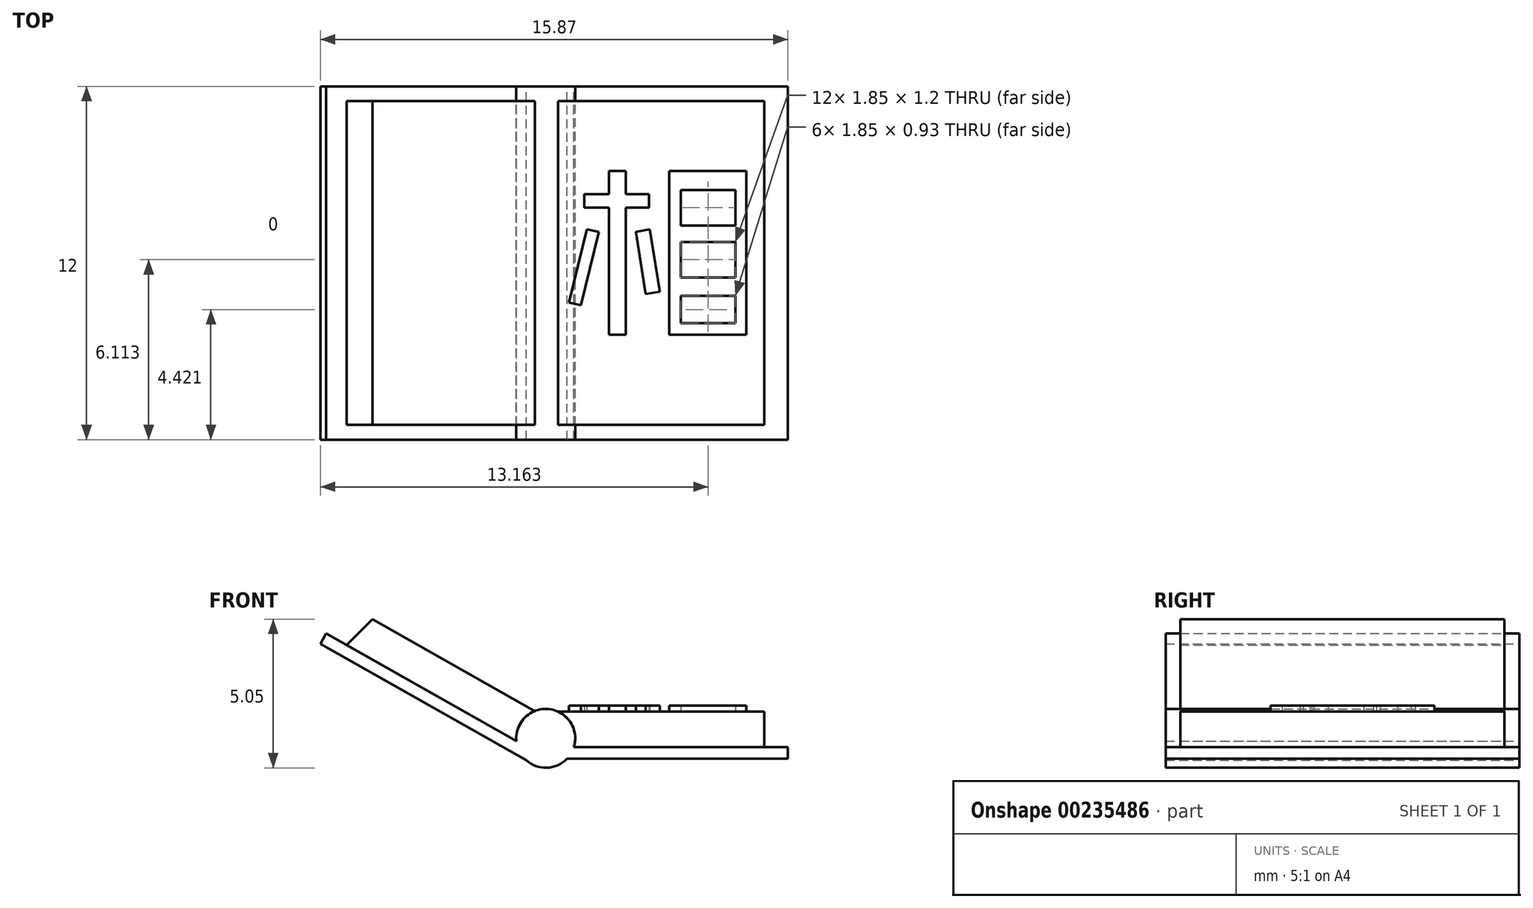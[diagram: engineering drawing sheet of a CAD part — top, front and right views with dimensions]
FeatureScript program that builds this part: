
annotation { "Feature Type Name" : "Feature", "Feature Type Description" : "" }
export const myFeature = defineFeature(function(context is Context, id is Id, definition is map)
    precondition{}
    {
        {
            var Q0;
            Q0=qCreatedBy(makeId("Front.planeOp"),FACE);
            var sketch = newSketch(context, id + "F0", { "sketchPlane" : qUnion([Q0])});
            skLineSegment(sketch, "E0", {"start": v(0.72, 0) * mm, "end": v(8.22, 0) * mm});
            skLineSegment(sketch, "E1", {"start": v(8.22, 0) * mm, "end": v(8.22, 0.4) * mm});
            skLineSegment(sketch, "E2", {"start": v(8.22, 0.4) * mm, "end": v(7.42, 0.4) * mm});
            skLineSegment(sketch, "E3", {"start": v(7.42, 0.4) * mm, "end": v(7.42, 1.6) * mm});
            skLineSegment(sketch, "E4", {"start": v(7.42, 1.6) * mm, "end": v(0.42, 1.6) * mm});
            skCircle(sketch, "E5", {"center": v(0, 0.7) * mm, "radius": 1 * mm});
            skPoint(sketch, "E6.orphan", {"position": v(0, 0) * mm});
            skLineSegment(sketch, "E7", {"start": v(7.42, 0.4) * mm, "end": v(0.96, 0.4) * mm});
            skLineSegment(sketch, "E8", {"start": v(7.42, 0.8) * mm, "end": v(1, 0.8) * mm});
            skLineSegment(sketch, "E9", {"start": v(7.42, 1.2) * mm, "end": v(0.86, 1.2) * mm});
            skLineSegment(sketch, "E10.1.0", {"start": v(-6.46, 4.15) * mm, "end": v(-0.94, 1.02) * mm});
            skLineSegment(sketch, "E10.1.2", {"start": v(-6.17, 4.45) * mm, "end": v(-0.74, 1.37) * mm});
            skLineSegment(sketch, "E10.1.3", {"start": v(-5.88, 4.74) * mm, "end": v(-0.37, 1.62) * mm});
            skLineSegment(sketch, "E10.1.5", {"start": v(-6.76, 3.86) * mm, "end": v(-1, 0.6) * mm});
            skLineSegment(sketch, "E10.1.8", {"start": v(-5.88, 4.74) * mm, "end": v(-6.76, 3.86) * mm});
            skLineSegment(sketch, "E10.anchor1", {"start": v(0, 0.7) * mm, "end": v(0.72, 0) * mm, "construction": true});
            skLineSegment(sketch, "E10.anchor2", {"start": v(0, 0.7) * mm, "end": v(-0.97, 0.93) * mm, "construction": true});
            skLineSegment(sketch, "E11.1.0", {"start": v(-0.67, -0.05) * mm, "end": v(-7.65, 3.9) * mm});
            skLineSegment(sketch, "E12", {"start": v(-6.76, 3.86) * mm, "end": v(-7.45, 4.25) * mm});
            skLineSegment(sketch, "E13", {"start": v(-7.45, 4.25) * mm, "end": v(-7.65, 3.9) * mm});
            skSolve(sketch);
        }
        {
            var Q0;
            {var subQ0=sQuery(id+"F0.wireOp",EDGE,"E5");var subQ5=makeQuery(id+"F0.imprint","INTERSECT",VERTEX,{"derivedFrom":[subQ0,sQuery(id+"F0.wireOp",EDGE,"E8")]});Q0=makeQuery(id+"F0.imprint","IMPRINT",FACE,{"disambiguationData":[TD([[makeQuery(id+"F0.imprint","IMPRINT",EDGE,{"disambiguationData":[TD([[subQ5,-1.0]])],"derivedFrom":subQ0}),1.0]])]});}
            var Q1;
            {var subQ1=sQuery(id+"F0.wireOp",EDGE,"E0");Q1=makeQuery(id+"F0.imprint","IMPRINT",FACE,{"disambiguationData":[TD([[makeQuery(id+"F0.imprint","IMPRINT",EDGE,{"derivedFrom":subQ1}),1.0]])]});}
            var Q2;
            {var subQ0=sQuery(id+"F0.wireOp",EDGE,"E10.1.5");Q2=makeQuery(id+"F0.imprint","IMPRINT",FACE,{"disambiguationData":[TD([[makeQuery(id+"F0.imprint","IMPRINT",EDGE,{"derivedFrom":subQ0}),-1.0]])]});}
            extrude(context, id + "F1", {"entities" : qUnion([Q0, Q1, Q2]), "depth" : 12 * mm});
        }
        {
            var Q0;
            {var subQ0=sQuery(id+"F0.wireOp",EDGE,"E7");Q0=makeQuery(id+"F0.imprint","IMPRINT",FACE,{"disambiguationData":[TD([[makeQuery(id+"F0.imprint","IMPRINT",EDGE,{"derivedFrom":subQ0}),-1.0]])]});}
            var Q1;
            {var subQ0=sQuery(id+"F0.wireOp",EDGE,"E8");Q1=makeQuery(id+"F0.imprint","IMPRINT",FACE,{"disambiguationData":[TD([[makeQuery(id+"F0.imprint","IMPRINT",EDGE,{"derivedFrom":subQ0}),-1.0]])]});}
            var Q2;
            {var subQ0=sQuery(id+"F0.wireOp",EDGE,"E4");Q2=makeQuery(id+"F0.imprint","IMPRINT",FACE,{"disambiguationData":[TD([[makeQuery(id+"F0.imprint","IMPRINT",EDGE,{"derivedFrom":subQ0}),1.0]])]});}
            var Q3;
            {var subQ0=sQuery(id+"F0.wireOp",EDGE,"E10.1.0");Q3=makeQuery(id+"F0.imprint","IMPRINT",FACE,{"disambiguationData":[TD([[makeQuery(id+"F0.imprint","IMPRINT",EDGE,{"derivedFrom":subQ0}),-1.0]])]});}
            var Q4;
            {var subQ0=sQuery(id+"F0.wireOp",EDGE,"E10.1.0");Q4=makeQuery(id+"F0.imprint","IMPRINT",FACE,{"disambiguationData":[TD([[makeQuery(id+"F0.imprint","IMPRINT",EDGE,{"derivedFrom":subQ0}),1.0]])]});}
            var Q5;
            {var subQ0=sQuery(id+"F0.wireOp",EDGE,"E10.1.2");Q5=makeQuery(id+"F0.imprint","IMPRINT",FACE,{"disambiguationData":[TD([[makeQuery(id+"F0.imprint","IMPRINT",EDGE,{"derivedFrom":subQ0}),1.0]])]});}
            extrude(context, id + "F2", {"entities" : qUnion([Q0, Q1, Q2, Q3, Q4, Q5]), "depth" : 11.5 * mm});
        }
        {
            var Q0;
            {var subQ0=sQuery(id+"F0.wireOp",EDGE,"E10.1.2");Q0=makeQuery(id+"F0.imprint","IMPRINT",FACE,{"disambiguationData":[TD([[makeQuery(id+"F0.imprint","IMPRINT",EDGE,{"derivedFrom":subQ0}),1.0]])]});}
            var Q1;
            {var subQ0=sQuery(id+"F0.wireOp",EDGE,"E10.1.0");Q1=makeQuery(id+"F0.imprint","IMPRINT",FACE,{"disambiguationData":[TD([[makeQuery(id+"F0.imprint","IMPRINT",EDGE,{"derivedFrom":subQ0}),1.0]])]});}
            var Q2;
            {var subQ0=sQuery(id+"F0.wireOp",EDGE,"E10.1.0");Q2=makeQuery(id+"F0.imprint","IMPRINT",FACE,{"disambiguationData":[TD([[makeQuery(id+"F0.imprint","IMPRINT",EDGE,{"derivedFrom":subQ0}),-1.0]])]});}
            var Q3;
            {var subQ0=sQuery(id+"F0.wireOp",EDGE,"E4");Q3=makeQuery(id+"F0.imprint","IMPRINT",FACE,{"disambiguationData":[TD([[makeQuery(id+"F0.imprint","IMPRINT",EDGE,{"derivedFrom":subQ0}),1.0]])]});}
            var Q4;
            {var subQ0=sQuery(id+"F0.wireOp",EDGE,"E8");Q4=makeQuery(id+"F0.imprint","IMPRINT",FACE,{"disambiguationData":[TD([[makeQuery(id+"F0.imprint","IMPRINT",EDGE,{"derivedFrom":subQ0}),-1.0]])]});}
            var Q5;
            {var subQ0=sQuery(id+"F0.wireOp",EDGE,"E7");Q5=makeQuery(id+"F0.imprint","IMPRINT",FACE,{"disambiguationData":[TD([[makeQuery(id+"F0.imprint","IMPRINT",EDGE,{"derivedFrom":subQ0}),-1.0]])]});}
            extrude(context, id + "F3", {"entities" : qUnion([Q0, Q1, Q2, Q3, Q4, Q5]), "operationType" : NewBodyOperationType.REMOVE, "depth" : 0.5 * mm});
        }
        {
            var Q0;
            Q0=makeQuery(id+"F2.opExtrude","SWEPT_FACE",FACE,{"disambiguationData":[OSD([sQuery(id+"F0.wireOp",EDGE,"E4")])]});
            cPlane(context, id + "F4", {"entities" : qUnion([Q0]), "cplaneType" : CPlaneType.OFFSET, "offset" : 0 * mm, "width" : 150 * mm, "height" : 150 * mm});
        }
        {
            var Q0;
            Q0=qCreatedBy(id+"F4.planeOp",FACE);
            var sketch = newSketch(context, id + "F5", { "sketchPlane" : qUnion([Q0])});
            skLineSegment(sketch, "E14.bottom", {"start": v(2.14, -2.88) * mm, "end": v(2.72, -2.88) * mm});
            skLineSegment(sketch, "E14.top", {"start": v(2.14, -8.44) * mm, "end": v(2.72, -8.44) * mm});
            skLineSegment(sketch, "E14.left", {"start": v(2.14, -2.88) * mm, "end": v(2.14, -3.67) * mm});
            skLineSegment(sketch, "E14.right", {"start": v(2.72, -2.88) * mm, "end": v(2.72, -3.67) * mm});
            skLineSegment(sketch, "E15.bottom", {"start": v(1.3, -3.67) * mm, "end": v(2.14, -3.67) * mm});
            skLineSegment(sketch, "E15.top", {"start": v(1.3, -4.12) * mm, "end": v(2.14, -4.12) * mm});
            skLineSegment(sketch, "E15.left", {"start": v(1.3, -3.67) * mm, "end": v(1.3, -4.12) * mm});
            skLineSegment(sketch, "E15.right", {"start": v(3.51, -3.67) * mm, "end": v(3.51, -4.12) * mm});
            skLineSegment(sketch, "E16", {"start": v(1.4, -4.85) * mm, "end": v(0.8, -7.34) * mm});
            skLineSegment(sketch, "E17", {"start": v(0.8, -7.34) * mm, "end": v(1.2, -7.44) * mm});
            skLineSegment(sketch, "E18", {"start": v(1.2, -7.44) * mm, "end": v(1.8, -4.95) * mm});
            skLineSegment(sketch, "E19", {"start": v(1.8, -4.95) * mm, "end": v(1.4, -4.85) * mm});
            skLineSegment(sketch, "E20", {"start": v(3.05, -4.95) * mm, "end": v(3.39, -7.05) * mm});
            skLineSegment(sketch, "E21", {"start": v(3.39, -7.05) * mm, "end": v(3.87, -6.97) * mm});
            skLineSegment(sketch, "E22", {"start": v(3.87, -6.97) * mm, "end": v(3.54, -4.85) * mm});
            skLineSegment(sketch, "E23", {"start": v(3.54, -4.85) * mm, "end": v(3.05, -4.95) * mm});
            skPoint(sketch, "E24.firstSnap0", {"position": v(2.43, -2.88) * mm});
            skLineSegment(sketch, "E24.bottom", {"start": v(4.2, -2.88) * mm, "end": v(6.81, -2.88) * mm});
            skLineSegment(sketch, "E24.top", {"start": v(4.2, -8.44) * mm, "end": v(6.81, -8.44) * mm});
            skLineSegment(sketch, "E24.left", {"start": v(4.2, -2.88) * mm, "end": v(4.2, -8.44) * mm});
            skLineSegment(sketch, "E24.right", {"start": v(6.81, -2.88) * mm, "end": v(6.81, -8.44) * mm});
            skLineSegment(sketch, "E25.bottom", {"start": v(4.59, -3.52) * mm, "end": v(6.44, -3.52) * mm});
            skLineSegment(sketch, "E25.top", {"start": v(4.59, -4.72) * mm, "end": v(6.44, -4.72) * mm});
            skLineSegment(sketch, "E25.left", {"start": v(4.59, -3.52) * mm, "end": v(4.59, -4.72) * mm});
            skLineSegment(sketch, "E25.right", {"start": v(6.44, -3.52) * mm, "end": v(6.44, -4.72) * mm});
            skLineSegment(sketch, "E26.bottom", {"start": v(4.59, -5.29) * mm, "end": v(6.44, -5.29) * mm});
            skLineSegment(sketch, "E26.top", {"start": v(4.59, -6.49) * mm, "end": v(6.44, -6.49) * mm});
            skLineSegment(sketch, "E26.left", {"start": v(4.59, -5.29) * mm, "end": v(4.59, -6.49) * mm});
            skLineSegment(sketch, "E26.right", {"start": v(6.44, -5.29) * mm, "end": v(6.44, -6.49) * mm});
            skLineSegment(sketch, "E27.bottom", {"start": v(4.59, -7.11) * mm, "end": v(6.44, -7.11) * mm});
            skLineSegment(sketch, "E27.top", {"start": v(4.59, -8.05) * mm, "end": v(6.44, -8.05) * mm});
            skLineSegment(sketch, "E27.left", {"start": v(4.59, -7.11) * mm, "end": v(4.59, -8.05) * mm});
            skLineSegment(sketch, "E27.right", {"start": v(6.44, -7.11) * mm, "end": v(6.44, -8.05) * mm});
            skLineSegment(sketch, "E28.trimOffspring", {"start": v(2.72, -4.12) * mm, "end": v(2.72, -8.44) * mm});
            skLineSegment(sketch, "E29.trimOffspring", {"start": v(2.14, -4.12) * mm, "end": v(2.14, -8.44) * mm});
            skLineSegment(sketch, "E30.trimOffspring", {"start": v(2.72, -3.67) * mm, "end": v(3.51, -3.67) * mm});
            skLineSegment(sketch, "E31.trimOffspring", {"start": v(2.72, -4.12) * mm, "end": v(3.51, -4.12) * mm});
            skSolve(sketch);
        }
        {
            var Q0;
            Q0=makeQuery(id+"F5.imprint","IMPRINT",FACE,{"disambiguationData":[TD([[makeQuery(id+"F5.imprint","IMPRINT",EDGE,{"derivedFrom":sQuery(id+"F5.wireOp",EDGE,"E16")}),1.0]])]});
            var Q1;
            Q1=makeQuery(id+"F5.imprint","IMPRINT",FACE,{"disambiguationData":[TD([[makeQuery(id+"F5.imprint","IMPRINT",EDGE,{"derivedFrom":sQuery(id+"F5.wireOp",EDGE,"E14.bottom")}),-1.0]])]});
            var Q2;
            Q2=makeQuery(id+"F5.imprint","IMPRINT",FACE,{"disambiguationData":[TD([[makeQuery(id+"F5.imprint","IMPRINT",EDGE,{"derivedFrom":sQuery(id+"F5.wireOp",EDGE,"E20")}),1.0]])]});
            var Q3;
            Q3=makeQuery(id+"F5.imprint","IMPRINT",FACE,{"disambiguationData":[TD([[makeQuery(id+"F5.imprint","IMPRINT",EDGE,{"derivedFrom":sQuery(id+"F5.wireOp",EDGE,"E24.bottom")}),-1.0]])]});
            extrude(context, id + "F6", {"entities" : qUnion([Q0, Q1, Q2, Q3]), "depth" : 0.2 * mm});
        }
    });
